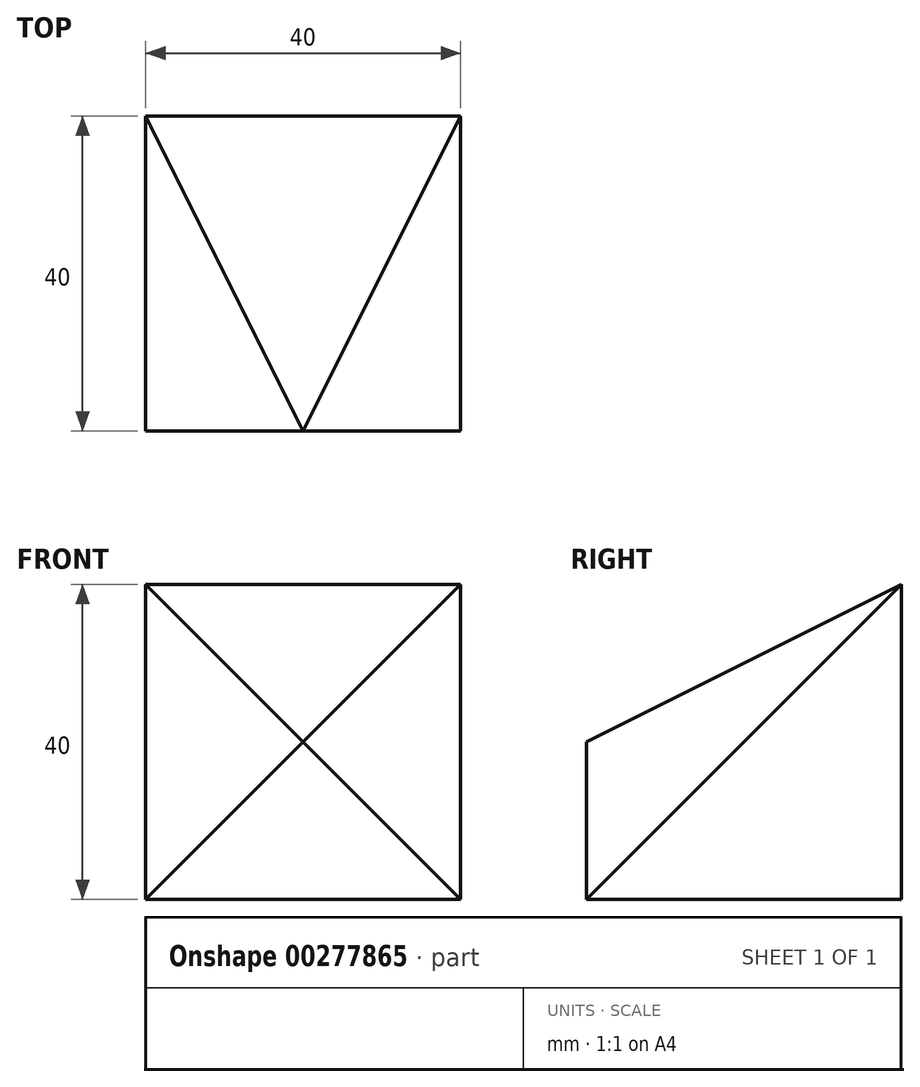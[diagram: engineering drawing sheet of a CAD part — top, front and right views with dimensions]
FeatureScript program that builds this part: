
annotation { "Feature Type Name" : "Feature", "Feature Type Description" : "" }
export const myFeature = defineFeature(function(context is Context, id is Id, definition is map)
    precondition{}
    {
        {
            var Q0;
            Q0=qCreatedBy(makeId("Right.planeOp"),FACE);
            var sketch = newSketch(context, id + "F0", { "sketchPlane" : qUnion([Q0])});
            skLineSegment(sketch, "E0.bottom", {"start": v(0, 0) * mm, "end": v(40, 0) * mm});
            skLineSegment(sketch, "E0.top", {"start": v(0, 40) * mm, "end": v(40, 40) * mm});
            skLineSegment(sketch, "E0.left", {"start": v(0, 0) * mm, "end": v(0, 40) * mm});
            skLineSegment(sketch, "E0.right", {"start": v(40, 0) * mm, "end": v(40, 40) * mm});
            skLineSegment(sketch, "E1", {"start": v(0, 20) * mm, "end": v(40, 40) * mm});
            skSolve(sketch);
        }
        {
            var Q0;
            {var subQ0=sQuery(id+"F0.wireOp",EDGE,"E0.bottom");Q0=makeQuery(id+"F0.imprint","IMPRINT",FACE,{"disambiguationData":[TD([[makeQuery(id+"F0.imprint","IMPRINT",EDGE,{"derivedFrom":subQ0}),1.0]])]});}
            extrude(context, id + "F1", {"entities" : qUnion([Q0]), "depth" : 40 * mm, "symmetric" : true});
        }
        {
            var Q0;
            Q0=makeQuery(id+"F1.opExtrude","SWEPT_EDGE",EDGE,{"disambiguationData":[OSD([sQuery(id+"F0.wireOp",EDGE,"E0.left"),sQuery(id+"F0.wireOp",EDGE,"E1")])]});
            cPoint(context, id + "F2", {"entities" : qUnion([Q0]), "parameter" : 0.5});
        }
        {
            var Q0;
            Q0=makeQuery(id+"F1.opExtrude","CAP_VERTEX",VERTEX,{"disambiguationData":[OSD([sQuery(id+"F0.wireOp",EDGE,"E0.top"),sQuery(id+"F0.wireOp",EDGE,"E0.right"),sQuery(id+"F0.wireOp",EDGE,"E1")])],"isStart":false});
            var Q1;
            Q1=makeQuery(id+"F1.opExtrude","CAP_VERTEX",VERTEX,{"disambiguationData":[OSD([sQuery(id+"F0.wireOp",EDGE,"E0.bottom"),sQuery(id+"F0.wireOp",EDGE,"E0.left")])],"isStart":false});
            var Q2;
            Q2 = qCreatedBy(id + "F2" ,VERTEX);
            cPlane(context, id + "F3", {"entities" : qUnion([Q0, Q1, Q2]), "cplaneType" : CPlaneType.THREE_POINT, "offset" : 25 * mm, "width" : 150 * mm, "height" : 150 * mm});
        }
        {
            var Q0;
            Q0=qCreatedBy(id+"F3.planeOp",FACE);
            var sketch = newSketch(context, id + "F4", { "sketchPlane" : qUnion([Q0])});
            skLineSegment(sketch, "E2.bottom", {"start": v(-23.52, 62.52) * mm, "end": v(51.02, 62.52) * mm});
            skLineSegment(sketch, "E2.top", {"start": v(-23.52, -17.02) * mm, "end": v(51.02, -17.02) * mm});
            skLineSegment(sketch, "E2.left", {"start": v(-23.52, 62.52) * mm, "end": v(-23.52, -17.02) * mm});
            skLineSegment(sketch, "E2.right", {"start": v(51.02, 62.52) * mm, "end": v(51.02, -17.02) * mm});
            skSolve(sketch);
        }
        {
            var Q0;
            Q0 = qSketchRegion(id + "F4", true);
            extrude(context, id + "F5", {"entities" : qUnion([Q0]), "operationType" : NewBodyOperationType.REMOVE, "endBound" : BoundingType.THROUGH_ALL, "depth" : 25 * mm});
        }
        {
            var Q0;
            Q0=makeQuery(id+"F1.opExtrude","CAP_VERTEX",VERTEX,{"disambiguationData":[OSD([sQuery(id+"F0.wireOp",EDGE,"E0.top"),sQuery(id+"F0.wireOp",EDGE,"E0.right"),sQuery(id+"F0.wireOp",EDGE,"E1")])],"isStart":true});
            var Q1;
            Q1=makeQuery(id+"F5.boolean.opBoolean","INTERSECT",VERTEX,{"derivedFrom":[makeQuery(id+"F1.opExtrude","SWEPT_FACE",FACE,{"disambiguationData":[OSD([sQuery(id+"F0.wireOp",EDGE,"E0.left")])]}),makeQuery(id+"F1.opExtrude","SWEPT_FACE",FACE,{"disambiguationData":[OSD([sQuery(id+"F0.wireOp",EDGE,"E1")])]}),makeQuery(id+"F5.opExtrude","CAP_FACE",FACE,{"disambiguationData":[OSD([sQuery(id+"F4.wireOp",EDGE,"E2.bottom"),sQuery(id+"F4.wireOp",EDGE,"E2.top"),sQuery(id+"F4.wireOp",EDGE,"E2.left"),sQuery(id+"F4.wireOp",EDGE,"E2.right")])],"isStart":true})]});
            var Q2;
            Q2=makeQuery(id+"F1.opExtrude","CAP_VERTEX",VERTEX,{"disambiguationData":[OSD([sQuery(id+"F0.wireOp",EDGE,"E0.bottom"),sQuery(id+"F0.wireOp",EDGE,"E0.left")])],"isStart":true});
            cPlane(context, id + "F6", {"entities" : qUnion([Q0, Q1, Q2]), "cplaneType" : CPlaneType.THREE_POINT, "offset" : 25 * mm, "width" : 150 * mm, "height" : 150 * mm});
        }
        {
            var Q0;
            Q0=qCreatedBy(id+"F6.planeOp",FACE);
            var sketch = newSketch(context, id + "F7", { "sketchPlane" : qUnion([Q0])});
            skLineSegment(sketch, "E3.bottom", {"start": v(-41.13, 67.77) * mm, "end": v(21.03, 67.77) * mm});
            skLineSegment(sketch, "E3.top", {"start": v(-41.13, -10.9) * mm, "end": v(21.03, -10.9) * mm});
            skLineSegment(sketch, "E3.left", {"start": v(-41.13, 67.77) * mm, "end": v(-41.13, -10.9) * mm});
            skLineSegment(sketch, "E3.right", {"start": v(21.03, 67.77) * mm, "end": v(21.03, -10.9) * mm});
            skSolve(sketch);
        }
        {
            var Q0;
            Q0 = qSketchRegion(id + "F7", true);
            extrude(context, id + "F8", {"entities" : qUnion([Q0]), "operationType" : NewBodyOperationType.REMOVE, "depth" : 25 * mm});
        }
    });
